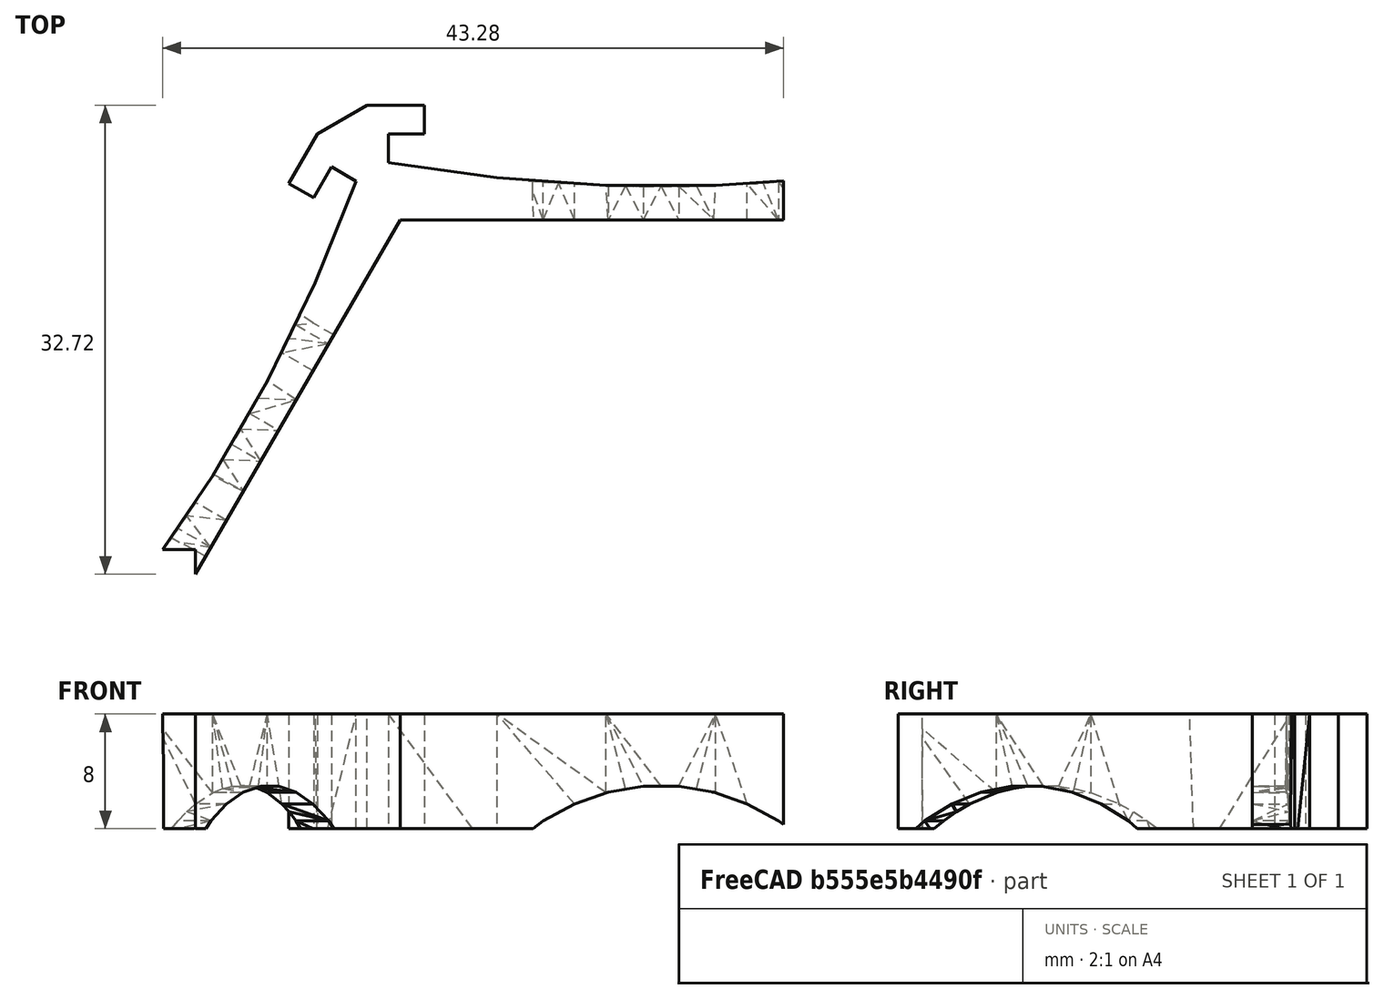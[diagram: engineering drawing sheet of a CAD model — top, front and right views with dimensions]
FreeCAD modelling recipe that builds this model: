
FCSTD DOCUMENT  (FreeCAD 0.16R)
Label: techo reparado exagono
License: All rights reserved
LicenseURL: http://en.wikipedia.org/wiki/All_rights_reserved
objects: Part::Box×6, Part::Cut×5, Part::Feature×2, Mesh::Feature×1, Part::MultiCommon×1
note: 14 computed .brp shape members not serialized (recipe doc carries the construction recipe); baked Part::Feature solids carry a one-line shape summary decoded from their .brp

FEATURE [Mesh::Feature] Nespresso_Hexagon_V1
FEATURE [Part::Feature] Nespresso_Hexagon_V1001
  shape: bbox 88.93 x 79.01 x 172 mm, 1796 faces, 0 solids (baked)
FEATURE [Part::Feature] Nespresso_Hexagon_V1001_solid  label="Nespresso_Hexagon_V1001 (Solid)"
  shape: bbox 88.93 x 79.01 x 172 mm, 1796 faces (baked)
FEATURE [Part::Box] Box  label="Cubo"
  Height = 156
  Length = 98
  Placement = pos=(-5,-4,-4) rot=(0,0,1;0rad)
  Width = 88
FEATURE [Part::Cut] Cut
  Base = -> Nespresso_Hexagon_V1001_solid
  Placement = pos=(3,-1,-151) rot=(0,0,1;0rad)
  Tool = -> Box
FEATURE [Part::Box] Box001  label="Cubo001"
  Height = 31
  Length = 117
  Placement = pos=(-8,0,0) rot=(0,0,1;0rad)
  Width = 45
FEATURE [Part::Cut] Cut001
  Base = -> Cut
  Tool = -> Box001
FEATURE [Part::Box] Box002  label="Cubo002"
  Height = 25
  Length = 93
  Placement = pos=(-1,-5,0) rot=(0,0,1;0rad)
  Width = 12
FEATURE [Part::Cut] Cut002
  Base = -> Cut001
  Tool = -> Box002
FEATURE [Part::Box] Box003  label="Cubo003"
  Height = 29
  Length = 10
  Placement = pos=(5,37,-3) rot=(0,0,1;0rad)
  Width = 10
FEATURE [Part::Cut] Cut003
  Base = -> Cut002
  Tool = -> Box003
FEATURE [Part::Box] Box004  label="Cubo004"
  Height = 28
  Length = 40
  Placement = pos=(56,1,-2) rot=(0,0,1;0rad)
  Width = 92
FEATURE [Part::Cut] Cut004
  Base = -> Cut003
  Tool = -> Box004
FEATURE [Part::Box] Box005  label="Cubo005"
  Height = 10
  Length = 49
  Placement = pos=(9,35,13) rot=(0,0,1;0rad)
  Width = 53
FEATURE [Part::MultiCommon] Common
  Shapes = -> [Cut004,Box005]
